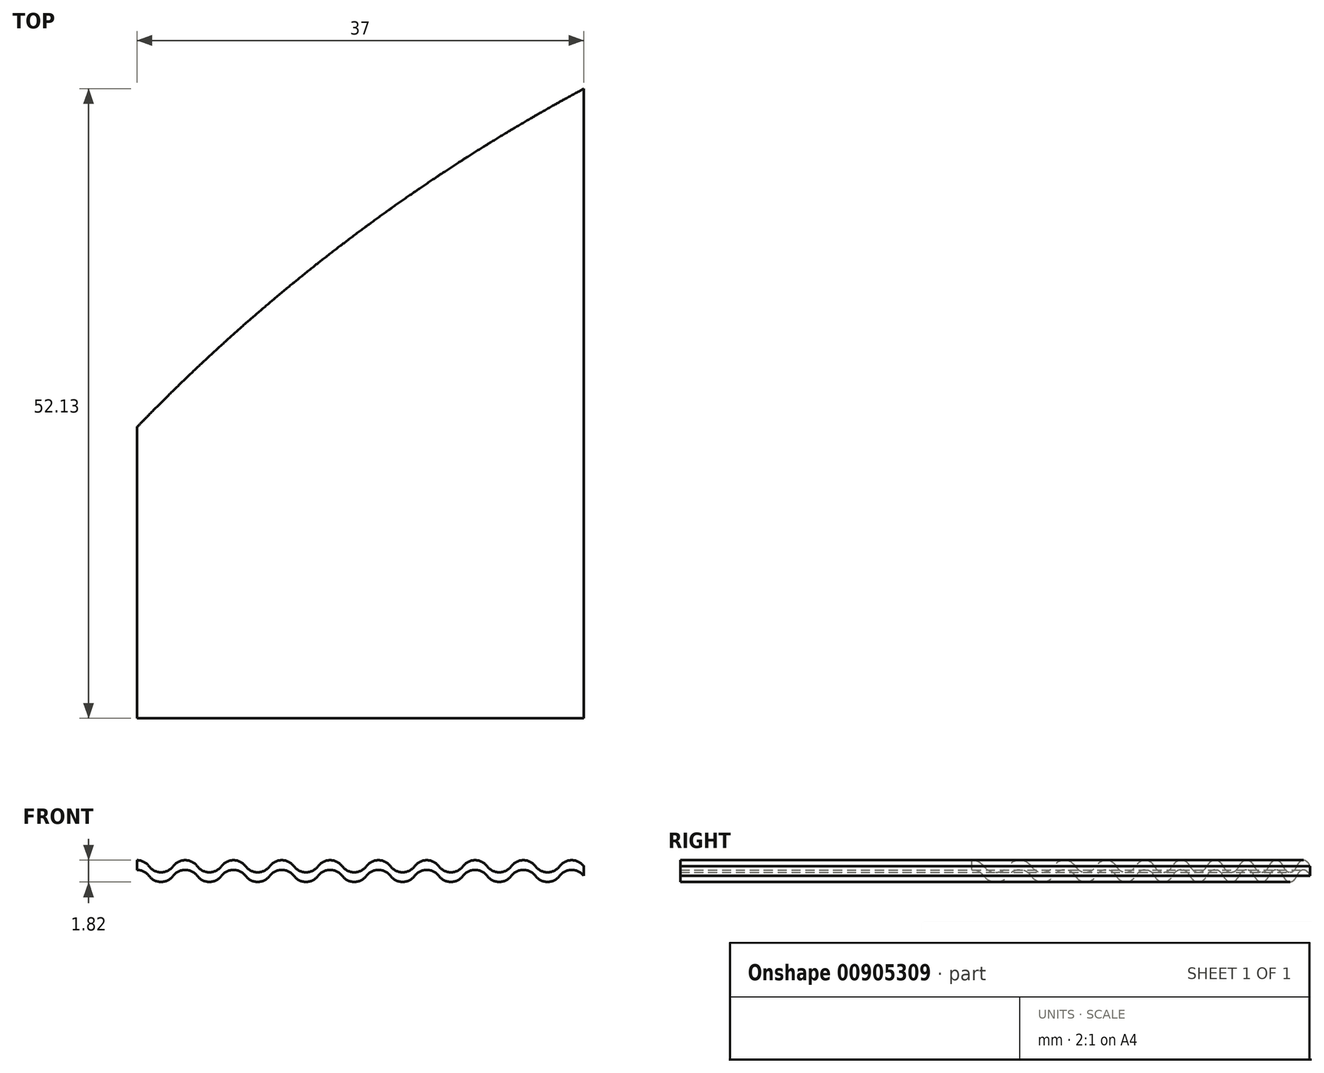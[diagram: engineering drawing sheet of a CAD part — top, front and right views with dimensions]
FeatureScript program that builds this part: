
annotation { "Feature Type Name" : "Feature", "Feature Type Description" : "" }
export const myFeature = defineFeature(function(context is Context, id is Id, definition is map)
    precondition{}
    {
        {
            var Q0;
            Q0=qCreatedBy(makeId("Front.planeOp"),FACE);
            var sketch = newSketch(context, id + "F0", { "sketchPlane" : qUnion([Q0])});
            skArc(sketch, "E0", {"start": v(-19, -0.4) * mm, "mid": v(-20, 0.1) * mm, "end": v(-21, -0.4) * mm});
            skArc(sketch, "E1", {"start": v(-23, -0.4) * mm, "mid": v(-22, -0.9) * mm, "end": v(-21, -0.4) * mm});
            skArc(sketch, "E2", {"start": v(-23, -0.4) * mm, "mid": v(-24, 0.1) * mm, "end": v(-25, -0.4) * mm});
            skArc(sketch, "E3", {"start": v(5, -0.4) * mm, "mid": v(6, -0.9) * mm, "end": v(7, -0.4) * mm});
            skArc(sketch, "E4", {"start": v(9, -0.4) * mm, "mid": v(8, 0.1) * mm, "end": v(7, -0.4) * mm});
            skArc(sketch, "E5", {"start": v(9, -0.4) * mm, "mid": v(10, -0.9) * mm, "end": v(11, -0.4) * mm});
            skArc(sketch, "E6", {"start": v(13, -0.4) * mm, "mid": v(12, 0.1) * mm, "end": v(11, -0.4) * mm});
            skArc(sketch, "E7", {"start": v(13, -0.4) * mm, "mid": v(14, -0.9) * mm, "end": v(15, -0.4) * mm});
            skArc(sketch, "E8", {"start": v(17, -0.4) * mm, "mid": v(16, 0.1) * mm, "end": v(15, -0.4) * mm});
            skArc(sketch, "E9", {"start": v(25, -0.4) * mm, "mid": v(24, 0.1) * mm, "end": v(23, -0.4) * mm});
            skArc(sketch, "E10", {"start": v(21, -0.4) * mm, "mid": v(22, -0.9) * mm, "end": v(23, -0.4) * mm});
            skArc(sketch, "E11", {"start": v(21, -0.4) * mm, "mid": v(20, 0.1) * mm, "end": v(19, -0.4) * mm});
            skArc(sketch, "E12", {"start": v(17, -0.4) * mm, "mid": v(18, -0.9) * mm, "end": v(19, -0.4) * mm});
            skArc(sketch, "E13", {"start": v(5, -0.4) * mm, "mid": v(4, 0.1) * mm, "end": v(3, -0.4) * mm});
            skArc(sketch, "E14", {"start": v(1, -0.4) * mm, "mid": v(2, -0.9) * mm, "end": v(3, -0.4) * mm});
            skArc(sketch, "E15", {"start": v(1, -0.4) * mm, "mid": v(0, 0.1) * mm, "end": v(-1, -0.4) * mm});
            skArc(sketch, "E16", {"start": v(-3, -0.4) * mm, "mid": v(-2, -0.9) * mm, "end": v(-1, -0.4) * mm});
            skArc(sketch, "E17", {"start": v(-3, -0.4) * mm, "mid": v(-4, 0.1) * mm, "end": v(-5, -0.4) * mm});
            skArc(sketch, "E18", {"start": v(-7, -0.4) * mm, "mid": v(-6, -0.9) * mm, "end": v(-5, -0.4) * mm});
            skArc(sketch, "E19", {"start": v(-7, -0.4) * mm, "mid": v(-8, 0.1) * mm, "end": v(-9, -0.4) * mm});
            skArc(sketch, "E20", {"start": v(-11, -0.4) * mm, "mid": v(-10, -0.9) * mm, "end": v(-9, -0.4) * mm});
            skArc(sketch, "E21", {"start": v(-11, -0.4) * mm, "mid": v(-12, 0.1) * mm, "end": v(-13, -0.4) * mm});
            skArc(sketch, "E22", {"start": v(-15, -0.4) * mm, "mid": v(-14, -0.9) * mm, "end": v(-13, -0.4) * mm});
            skArc(sketch, "E23", {"start": v(-15, -0.4) * mm, "mid": v(-16, 0.1) * mm, "end": v(-17, -0.4) * mm});
            skArc(sketch, "E24", {"start": v(-19, -0.4) * mm, "mid": v(-18, -0.9) * mm, "end": v(-17, -0.4) * mm});
            skArc(sketch, "E25", {"start": v(-19, 0.4) * mm, "mid": v(-20, 0.9) * mm, "end": v(-21, 0.4) * mm});
            skArc(sketch, "E26", {"start": v(-23, 0.4) * mm, "mid": v(-22, -0.1) * mm, "end": v(-21, 0.4) * mm});
            skArc(sketch, "E27", {"start": v(-23, 0.4) * mm, "mid": v(-24, 0.9) * mm, "end": v(-25, 0.4) * mm});
            skArc(sketch, "E28", {"start": v(5, 0.4) * mm, "mid": v(6, -0.1) * mm, "end": v(7, 0.4) * mm});
            skArc(sketch, "E29", {"start": v(9, 0.4) * mm, "mid": v(8, 0.9) * mm, "end": v(7, 0.4) * mm});
            skArc(sketch, "E30", {"start": v(9, 0.4) * mm, "mid": v(10, -0.1) * mm, "end": v(11, 0.4) * mm});
            skArc(sketch, "E31", {"start": v(13, 0.4) * mm, "mid": v(12, 0.9) * mm, "end": v(11, 0.4) * mm});
            skArc(sketch, "E32", {"start": v(13, 0.4) * mm, "mid": v(14, -0.1) * mm, "end": v(15, 0.4) * mm});
            skArc(sketch, "E33", {"start": v(17, 0.4) * mm, "mid": v(16, 0.9) * mm, "end": v(15, 0.4) * mm});
            skArc(sketch, "E34", {"start": v(25, 0.4) * mm, "mid": v(24, 0.9) * mm, "end": v(23, 0.4) * mm});
            skArc(sketch, "E35", {"start": v(21, 0.4) * mm, "mid": v(22, -0.1) * mm, "end": v(23, 0.4) * mm});
            skArc(sketch, "E36", {"start": v(21, 0.4) * mm, "mid": v(20, 0.9) * mm, "end": v(19, 0.4) * mm});
            skArc(sketch, "E37", {"start": v(17, 0.4) * mm, "mid": v(18, -0.1) * mm, "end": v(19, 0.4) * mm});
            skArc(sketch, "E38", {"start": v(5, 0.4) * mm, "mid": v(4, 0.9) * mm, "end": v(3, 0.4) * mm});
            skArc(sketch, "E39", {"start": v(1, 0.4) * mm, "mid": v(2, -0.1) * mm, "end": v(3, 0.4) * mm});
            skArc(sketch, "E40", {"start": v(1, 0.4) * mm, "mid": v(0, 0.9) * mm, "end": v(-1, 0.4) * mm});
            skArc(sketch, "E41", {"start": v(-3, 0.4) * mm, "mid": v(-2, -0.1) * mm, "end": v(-1, 0.4) * mm});
            skArc(sketch, "E42", {"start": v(-3, 0.4) * mm, "mid": v(-4, 0.9) * mm, "end": v(-5, 0.4) * mm});
            skArc(sketch, "E43", {"start": v(-7, 0.4) * mm, "mid": v(-6, -0.1) * mm, "end": v(-5, 0.4) * mm});
            skArc(sketch, "E44", {"start": v(-7, 0.4) * mm, "mid": v(-8, 0.9) * mm, "end": v(-9, 0.4) * mm});
            skArc(sketch, "E45", {"start": v(-11, 0.4) * mm, "mid": v(-10, -0.1) * mm, "end": v(-9, 0.4) * mm});
            skArc(sketch, "E46", {"start": v(-11, 0.4) * mm, "mid": v(-12, 0.9) * mm, "end": v(-13, 0.4) * mm});
            skArc(sketch, "E47", {"start": v(-15, 0.4) * mm, "mid": v(-14, -0.1) * mm, "end": v(-13, 0.4) * mm});
            skArc(sketch, "E48", {"start": v(-15, 0.4) * mm, "mid": v(-16, 0.9) * mm, "end": v(-17, 0.4) * mm});
            skArc(sketch, "E49", {"start": v(-19, 0.4) * mm, "mid": v(-18, -0.1) * mm, "end": v(-17, 0.4) * mm});
            skLineSegment(sketch, "E50", {"start": v(-25, 0.4) * mm, "end": v(-25, -0.4) * mm});
            skLineSegment(sketch, "E51", {"start": v(25, 0.4) * mm, "end": v(25, -0.4) * mm});
            skSolve(sketch);
        }
        {
            var Q0;
            Q0=qSketchRegion(id+"F0",true);
            extrude(context, id + "F1", {"entities" : qUnion([Q0]), "depth" : 70 * mm, "offsetDistance" : 25 * mm});
        }
        {
            var Q0;
            Q0=qCreatedBy(makeId("Top.planeOp"),FACE);
            var sketch = newSketch(context, id + "F2", { "sketchPlane" : qUnion([Q0])});
            skLineSegment(sketch, "E52", {"start": v(0, 0) * mm, "end": v(0, -150) * mm, "construction": true});
            skCircle(sketch, "E53", {"center": v(96, -150) * mm, "radius": 150 * mm});
            skLineSegment(sketch, "E54", {"start": v(96, -150) * mm, "end": v(0, -150) * mm, "construction": true});
            skLineSegment(sketch, "E55", {"start": v(96, -150) * mm, "end": v(-122.84, -150) * mm, "construction": true});
            skLineSegment(sketch, "E56", {"start": v(96, -150) * mm, "end": v(24, -150) * mm, "construction": true});
            skLineSegment(sketch, "E57", {"start": v(24, -150) * mm, "end": v(-12, -150) * mm, "construction": true});
            skLineSegment(sketch, "E58", {"start": v(-12, -150) * mm, "end": v(-12, -38.63) * mm});
            skLineSegment(sketch, "E59", {"start": v(-12, -38.63) * mm, "end": v(-12, -291.48) * mm});
            skSolve(sketch);
        }
        {
            var Q0;
            {var subQ0=sQuery(id+"F2.wireOp",EDGE,"E58");var subQ1=sQuery(id+"F2.wireOp",EDGE,"E53");var subQ2=makeQuery(id+"F2.imprint","INTERSECT",VERTEX,{"derivedFrom":[subQ1,subQ0]});Q0=makeQuery(id+"F2.imprint","IMPRINT",FACE,{"disambiguationData":[TD([[makeQuery(id+"F2.imprint","IMPRINT",EDGE,{"disambiguationData":[TD([[subQ2,1.0]])],"derivedFrom":subQ1}),1.0]])]});}
            extrude(context, id + "F3", {"entities" : qUnion([Q0]), "operationType" : NewBodyOperationType.INTERSECT, "depth" : 25 * mm, "offsetDistance" : 25 * mm, "hasSecondDirection" : true, "secondDirectionOppositeDirection" : true, "secondDirectionDepth" : 25 * mm});
        }
    });
